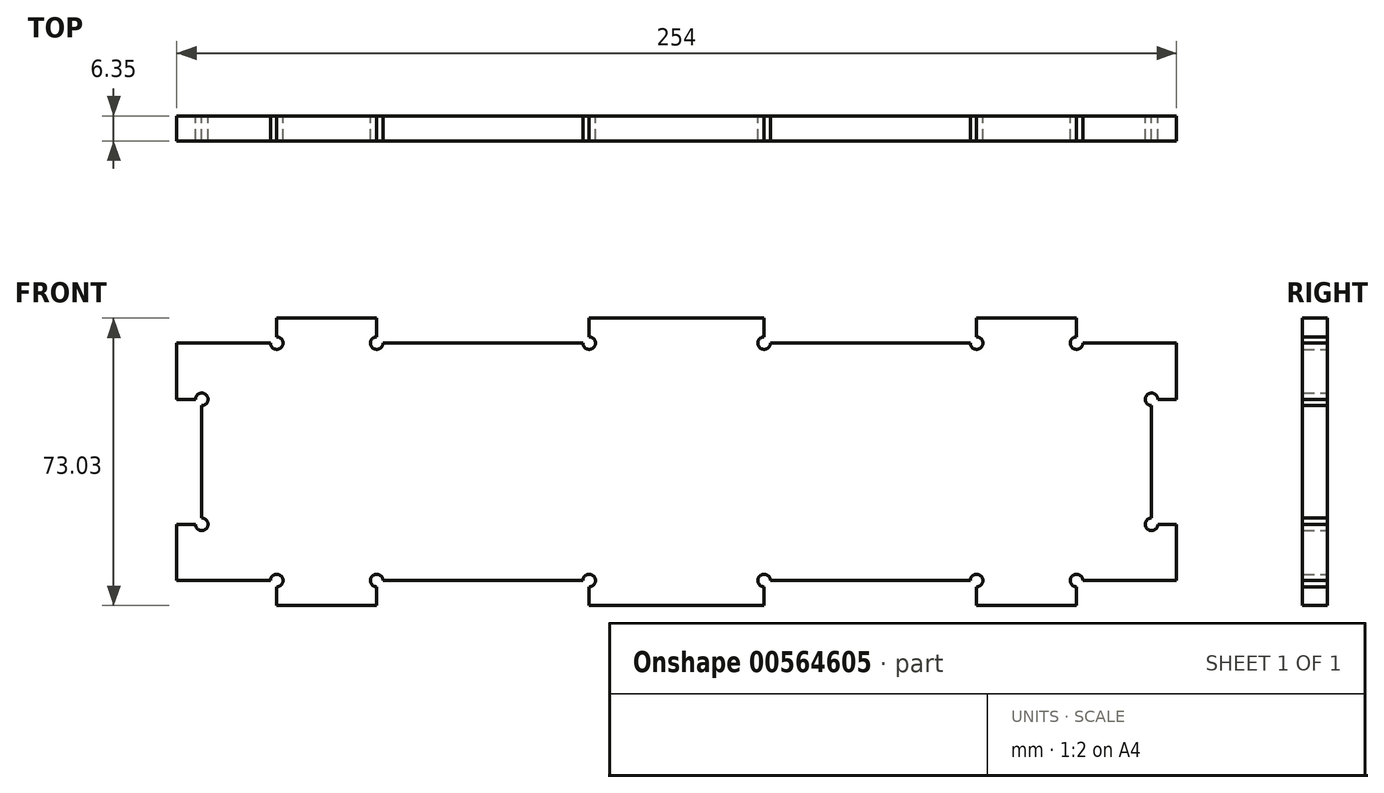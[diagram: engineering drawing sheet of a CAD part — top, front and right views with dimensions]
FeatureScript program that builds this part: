
annotation { "Feature Type Name" : "Feature", "Feature Type Description" : "" }
export const myFeature = defineFeature(function(context is Context, id is Id, definition is map)
    precondition{}
    {
        {
            var Q0;
            Q0=qCreatedBy(makeId("Front.planeOp"),FACE);
            var sketch = newSketch(context, id + "F0", { "sketchPlane" : qUnion([Q0])});
            skLineSegment(sketch, "E0.bottom", {"start": v(-121.97, 20.7) * mm, "end": v(132.03, 20.7) * mm});
            skLineSegment(sketch, "E0.top", {"start": v(-121.97, -39.63) * mm, "end": v(132.03, -39.63) * mm});
            skLineSegment(sketch, "E0.left", {"start": v(-121.97, 20.7) * mm, "end": v(-121.97, -39.63) * mm});
            skLineSegment(sketch, "E0.right", {"start": v(132.03, 20.7) * mm, "end": v(132.03, -39.63) * mm});
            skLineSegment(sketch, "E1.bottom", {"start": v(-96.57, 20.7) * mm, "end": v(-71.17, 20.7) * mm});
            skLineSegment(sketch, "E1.top", {"start": v(-96.57, 27.05) * mm, "end": v(-71.17, 27.05) * mm});
            skLineSegment(sketch, "E1.left", {"start": v(-96.57, 20.7) * mm, "end": v(-96.57, 27.05) * mm});
            skLineSegment(sketch, "E1.right", {"start": v(-71.17, 20.7) * mm, "end": v(-71.17, 27.05) * mm});
            skLineSegment(sketch, "E2.bottom", {"start": v(-17.2, 20.7) * mm, "end": v(27.26, 20.7) * mm});
            skLineSegment(sketch, "E2.top", {"start": v(-17.2, 27.05) * mm, "end": v(27.26, 27.05) * mm});
            skLineSegment(sketch, "E2.left", {"start": v(-17.2, 20.7) * mm, "end": v(-17.2, 27.05) * mm});
            skLineSegment(sketch, "E2.right", {"start": v(27.26, 20.7) * mm, "end": v(27.26, 27.05) * mm});
            skLineSegment(sketch, "E3.bottom", {"start": v(81.23, 20.7) * mm, "end": v(106.63, 20.7) * mm});
            skLineSegment(sketch, "E3.top", {"start": v(81.23, 27.05) * mm, "end": v(106.63, 27.05) * mm});
            skLineSegment(sketch, "E3.left", {"start": v(81.23, 20.7) * mm, "end": v(81.23, 27.05) * mm});
            skLineSegment(sketch, "E3.right", {"start": v(106.63, 20.7) * mm, "end": v(106.63, 27.05) * mm});
            skLineSegment(sketch, "E4.bottom", {"start": v(-121.97, 6.41) * mm, "end": v(-115.62, 6.41) * mm});
            skLineSegment(sketch, "E4.top", {"start": v(-121.97, -25.34) * mm, "end": v(-115.62, -25.34) * mm});
            skLineSegment(sketch, "E4.left", {"start": v(-121.97, 6.41) * mm, "end": v(-121.97, -25.34) * mm});
            skLineSegment(sketch, "E4.right", {"start": v(-115.62, 6.41) * mm, "end": v(-115.62, -25.34) * mm});
            skLineSegment(sketch, "E5.bottom", {"start": v(-71.17, -39.63) * mm, "end": v(-96.57, -39.63) * mm});
            skLineSegment(sketch, "E5.top", {"start": v(-71.17, -45.98) * mm, "end": v(-96.57, -45.98) * mm});
            skLineSegment(sketch, "E5.left", {"start": v(-71.17, -39.63) * mm, "end": v(-71.17, -45.98) * mm});
            skLineSegment(sketch, "E5.right", {"start": v(-96.57, -39.63) * mm, "end": v(-96.57, -45.98) * mm});
            skLineSegment(sketch, "E6.bottom", {"start": v(27.26, -39.63) * mm, "end": v(-17.2, -39.63) * mm});
            skLineSegment(sketch, "E6.top", {"start": v(27.26, -45.98) * mm, "end": v(-17.2, -45.98) * mm});
            skLineSegment(sketch, "E6.left", {"start": v(27.26, -39.63) * mm, "end": v(27.26, -45.98) * mm});
            skLineSegment(sketch, "E6.right", {"start": v(-17.2, -39.63) * mm, "end": v(-17.2, -45.98) * mm});
            skLineSegment(sketch, "E7.bottom", {"start": v(106.63, -39.63) * mm, "end": v(81.23, -39.63) * mm});
            skLineSegment(sketch, "E7.top", {"start": v(106.63, -45.98) * mm, "end": v(81.23, -45.98) * mm});
            skLineSegment(sketch, "E7.left", {"start": v(106.63, -39.63) * mm, "end": v(106.63, -45.98) * mm});
            skLineSegment(sketch, "E7.right", {"start": v(81.23, -39.63) * mm, "end": v(81.23, -45.98) * mm});
            skLineSegment(sketch, "E8.bottom", {"start": v(132.03, 6.41) * mm, "end": v(125.68, 6.41) * mm});
            skLineSegment(sketch, "E8.top", {"start": v(132.03, -25.34) * mm, "end": v(125.68, -25.34) * mm});
            skLineSegment(sketch, "E8.left", {"start": v(132.03, 6.41) * mm, "end": v(132.03, -25.34) * mm});
            skLineSegment(sketch, "E8.right", {"start": v(125.68, 6.41) * mm, "end": v(125.68, -25.34) * mm});
            skCircle(sketch, "E9", {"center": v(-96.57, 20.7) * mm, "radius": 1.59 * mm});
            skCircle(sketch, "E10", {"center": v(-71.17, 20.7) * mm, "radius": 1.59 * mm});
            skCircle(sketch, "E11", {"center": v(-17.2, 20.7) * mm, "radius": 1.59 * mm});
            skCircle(sketch, "E12", {"center": v(27.26, 20.7) * mm, "radius": 1.59 * mm});
            skCircle(sketch, "E13", {"center": v(81.23, 20.7) * mm, "radius": 1.59 * mm});
            skCircle(sketch, "E14", {"center": v(125.68, 6.41) * mm, "radius": 1.59 * mm});
            skCircle(sketch, "E15", {"center": v(125.68, -25.34) * mm, "radius": 1.59 * mm});
            skCircle(sketch, "E16", {"center": v(106.63, -39.63) * mm, "radius": 1.59 * mm});
            skCircle(sketch, "E17", {"center": v(81.23, -39.63) * mm, "radius": 1.59 * mm});
            skCircle(sketch, "E18", {"center": v(27.26, -39.63) * mm, "radius": 1.59 * mm});
            skCircle(sketch, "E19", {"center": v(-17.2, -39.63) * mm, "radius": 1.59 * mm});
            skCircle(sketch, "E20", {"center": v(-71.17, -39.63) * mm, "radius": 1.59 * mm});
            skCircle(sketch, "E21", {"center": v(-115.62, -25.34) * mm, "radius": 1.59 * mm});
            skCircle(sketch, "E22", {"center": v(-115.62, 6.41) * mm, "radius": 1.59 * mm});
            skCircle(sketch, "E23", {"center": v(-96.57, -39.63) * mm, "radius": 1.59 * mm});
            skCircle(sketch, "E24", {"center": v(106.63, 20.7) * mm, "radius": 1.59 * mm});
            skSolve(sketch);
        }
        {
            var Q0;
            {var subQ1=sQuery(id+"F0.wireOp",EDGE,"E1.top");Q0=makeQuery(id+"F0.imprint","IMPRINT",FACE,{"disambiguationData":[TD([[makeQuery(id+"F0.imprint","IMPRINT",EDGE,{"derivedFrom":subQ1}),-1.0]])]});}
            var Q1;
            {var subQ16=sQuery(id+"F0.wireOp",EDGE,"E0.left");var subQ35=sQuery(id+"F0.wireOp",EDGE,"E0.bottom");var subQ59=makeQuery(id+"F0.imprint","INTERSECT",VERTEX,{"derivedFrom":[subQ35,subQ16]});Q1=makeQuery(id+"F0.imprint","IMPRINT",FACE,{"disambiguationData":[TD([[makeQuery(id+"F0.imprint","IMPRINT",EDGE,{"disambiguationData":[TD([[subQ59,-1.0]])],"derivedFrom":subQ35}),-1.0]])]});}
            var Q2;
            {var subQ1=sQuery(id+"F0.wireOp",EDGE,"E2.top");Q2=makeQuery(id+"F0.imprint","IMPRINT",FACE,{"disambiguationData":[TD([[makeQuery(id+"F0.imprint","IMPRINT",EDGE,{"derivedFrom":subQ1}),-1.0]])]});}
            var Q3;
            {var subQ1=sQuery(id+"F0.wireOp",EDGE,"E3.top");Q3=makeQuery(id+"F0.imprint","IMPRINT",FACE,{"disambiguationData":[TD([[makeQuery(id+"F0.imprint","IMPRINT",EDGE,{"derivedFrom":subQ1}),-1.0]])]});}
            var Q4;
            {var subQ1=sQuery(id+"F0.wireOp",EDGE,"E7.top");Q4=makeQuery(id+"F0.imprint","IMPRINT",FACE,{"disambiguationData":[TD([[makeQuery(id+"F0.imprint","IMPRINT",EDGE,{"derivedFrom":subQ1}),-1.0]])]});}
            var Q5;
            {var subQ1=sQuery(id+"F0.wireOp",EDGE,"E6.top");Q5=makeQuery(id+"F0.imprint","IMPRINT",FACE,{"disambiguationData":[TD([[makeQuery(id+"F0.imprint","IMPRINT",EDGE,{"derivedFrom":subQ1}),-1.0]])]});}
            var Q6;
            {var subQ1=sQuery(id+"F0.wireOp",EDGE,"E5.top");Q6=makeQuery(id+"F0.imprint","IMPRINT",FACE,{"disambiguationData":[TD([[makeQuery(id+"F0.imprint","IMPRINT",EDGE,{"derivedFrom":subQ1}),-1.0]])]});}
            extrude(context, id + "F1", {"entities" : qUnion([Q0, Q1, Q2, Q3, Q4, Q5, Q6]), "depth" : 6.35 * mm, "offsetDistance" : 25.4 * mm});
        }
    });
